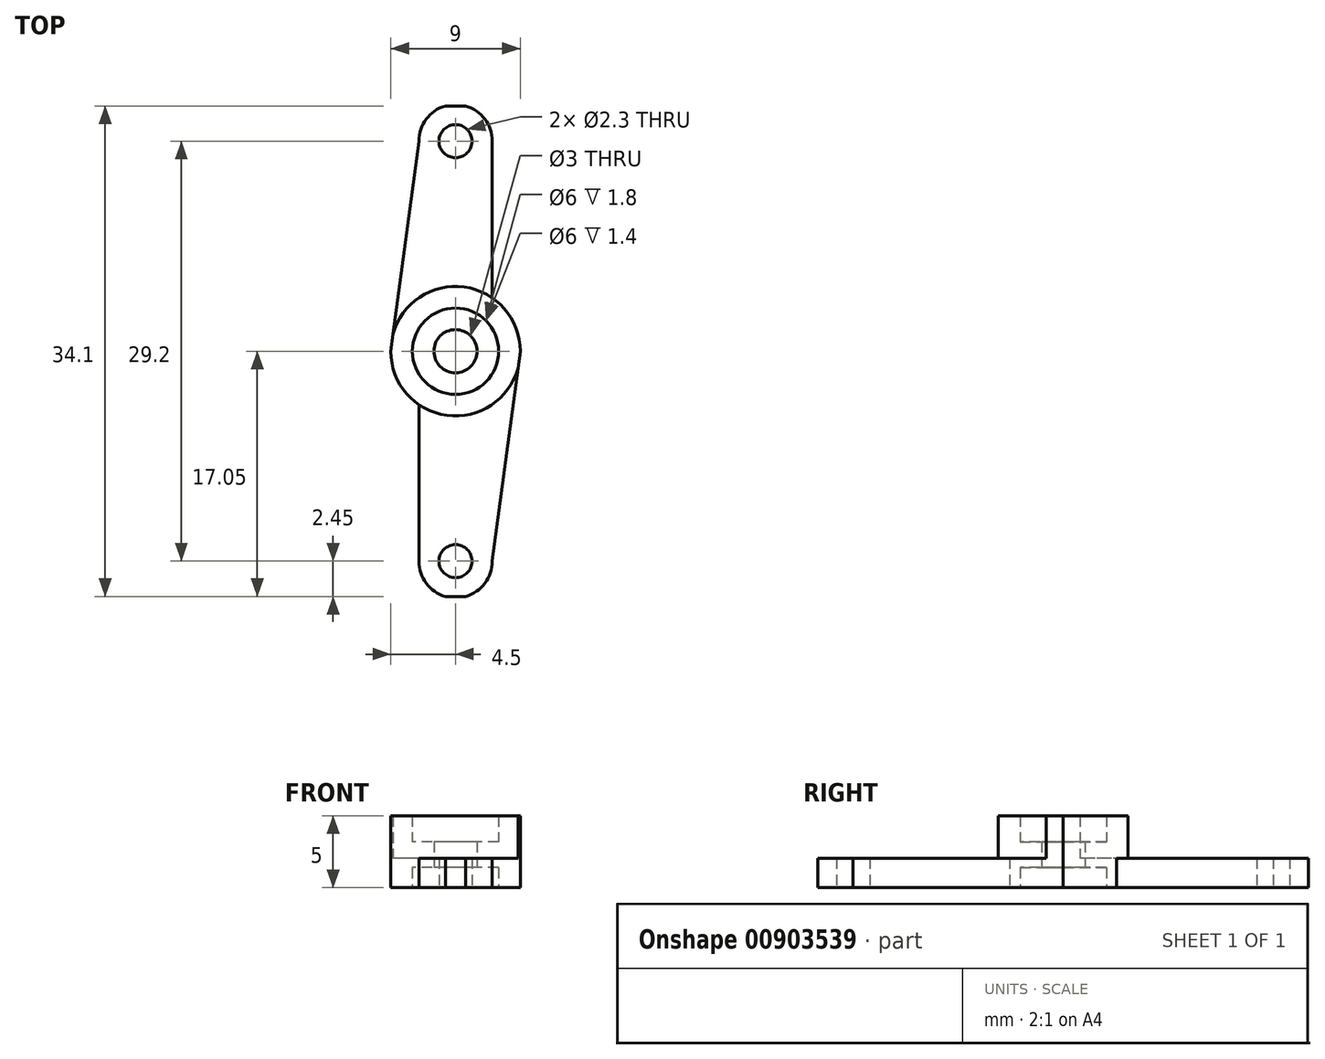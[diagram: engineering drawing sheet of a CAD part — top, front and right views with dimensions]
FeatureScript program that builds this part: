
annotation { "Feature Type Name" : "Feature", "Feature Type Description" : "" }
export const myFeature = defineFeature(function(context is Context, id is Id, definition is map)
    precondition{}
    {
        {
            var Q0;
            Q0=qCreatedBy(makeId("Top.planeOp"),FACE);
            var sketch = newSketch(context, id + "F0", { "sketchPlane" : qUnion([Q0])});
            skLineSegment(sketch, "E0.bottom", {"start": v(4.5, -17.05) * mm, "end": v(-4.5, -17.05) * mm});
            skLineSegment(sketch, "E0.top", {"start": v(4.5, 17.05) * mm, "end": v(-4.5, 17.05) * mm});
            skLineSegment(sketch, "E0.left", {"start": v(4.5, -17.05) * mm, "end": v(4.5, 17.05) * mm});
            skLineSegment(sketch, "E0.right", {"start": v(-4.5, -17.05) * mm, "end": v(-4.5, 17.05) * mm});
            skPoint(sketch, "E0.middle", {"position": v(0, 0) * mm});
            skCircle(sketch, "E1", {"center": v(0, 0) * mm, "radius": 4.5 * mm});
            skLineSegment(sketch, "E2", {"start": v(0, 0) * mm, "end": v(0, -14.6) * mm});
            skLineSegment(sketch, "E3", {"start": v(0, 0) * mm, "end": v(0, 14.6) * mm});
            skCircle(sketch, "E4", {"center": v(0, 14.6) * mm, "radius": 1.15 * mm});
            skCircle(sketch, "E5", {"center": v(0, -14.6) * mm, "radius": 1.15 * mm});
            skCircle(sketch, "E6.0", {"center": v(0, 14.6) * mm, "radius": 2.55 * mm});
            skCircle(sketch, "E7.0", {"center": v(0, -14.6) * mm, "radius": 2.55 * mm});
            skLineSegment(sketch, "E8", {"start": v(2.55, 14.6) * mm, "end": v(2.55, 3.7) * mm});
            skLineSegment(sketch, "E9", {"start": v(-2.55, -14.6) * mm, "end": v(-2.55, -3.7) * mm});
            skLineSegment(sketch, "E10", {"start": v(-2.55, -14.6) * mm, "end": v(2.55, -14.6) * mm, "construction": true});
            skLineSegment(sketch, "E11", {"start": v(2.55, 14.6) * mm, "end": v(-2.55, 14.6) * mm, "construction": true});
            skLineSegment(sketch, "E12", {"start": v(2.55, -14.6) * mm, "end": v(4.5, 0) * mm});
            skLineSegment(sketch, "E13", {"start": v(-2.55, 14.6) * mm, "end": v(-4.5, 0) * mm});
            skCircle(sketch, "E14", {"center": v(0, 0) * mm, "radius": 3 * mm});
            skCircle(sketch, "E15", {"center": v(0, 0) * mm, "radius": 1.5 * mm});
            skSolve(sketch);
        }
        {
            var Q0;
            {var subQ0=sQuery(id+"F0.wireOp",EDGE,"E2");var subQ1=sQuery(id+"F0.wireOp",EDGE,"E1");var subQ2=makeQuery(id+"F0.imprint","INTERSECT",VERTEX,{"derivedFrom":[subQ1,subQ0]});Q0=makeQuery(id+"F0.imprint","IMPRINT",FACE,{"disambiguationData":[TD([[makeQuery(id+"F0.imprint","IMPRINT",EDGE,{"disambiguationData":[TD([[subQ2,-1.0]])],"derivedFrom":subQ1}),-1.0]])]});}
            var Q1;
            Q1=makeQuery(id+"F0.imprint","IMPRINT",FACE,{"disambiguationData":[TD([[makeQuery(id+"F0.imprint","IMPRINT",EDGE,{"derivedFrom":sQuery(id+"F0.wireOp",EDGE,"E5")}),-1.0]])]});
            var Q2;
            {var subQ0=sQuery(id+"F0.wireOp",EDGE,"E9");Q2=makeQuery(id+"F0.imprint","IMPRINT",FACE,{"disambiguationData":[TD([[makeQuery(id+"F0.imprint","IMPRINT",EDGE,{"derivedFrom":subQ0}),-1.0]])]});}
            var Q3;
            {var subQ1=sQuery(id+"F0.wireOp",EDGE,"E1");var subQ8=sQuery(id+"F0.wireOp",EDGE,"E3");var subQ9=makeQuery(id+"F0.imprint","INTERSECT",VERTEX,{"derivedFrom":[subQ1,subQ8]});Q3=makeQuery(id+"F0.imprint","IMPRINT",FACE,{"disambiguationData":[TD([[makeQuery(id+"F0.imprint","IMPRINT",EDGE,{"disambiguationData":[TD([[subQ9,-1.0]])],"derivedFrom":subQ1}),1.0]])]});}
            var Q4;
            {var subQ0=sQuery(id+"F0.wireOp",EDGE,"E15");var subQ1=sQuery(id+"F0.wireOp",EDGE,"E2");var subQ2=makeQuery(id+"F0.imprint","INTERSECT",VERTEX,{"derivedFrom":[subQ1,subQ0]});Q4=makeQuery(id+"F0.imprint","IMPRINT",FACE,{"disambiguationData":[TD([[makeQuery(id+"F0.imprint","IMPRINT",EDGE,{"disambiguationData":[TD([[subQ2,-1.0]])],"derivedFrom":subQ1}),-1.0]])]});}
            var Q5;
            {var subQ0=sQuery(id+"F0.wireOp",EDGE,"E3");var subQ1=sQuery(id+"F0.wireOp",EDGE,"E1");var subQ2=makeQuery(id+"F0.imprint","INTERSECT",VERTEX,{"derivedFrom":[subQ1,subQ0]});Q5=makeQuery(id+"F0.imprint","IMPRINT",FACE,{"disambiguationData":[TD([[makeQuery(id+"F0.imprint","IMPRINT",EDGE,{"disambiguationData":[TD([[subQ2,-1.0]])],"derivedFrom":subQ1}),-1.0]])]});}
            var Q6;
            {var subQ0=sQuery(id+"F0.wireOp",EDGE,"E8");Q6=makeQuery(id+"F0.imprint","IMPRINT",FACE,{"disambiguationData":[TD([[makeQuery(id+"F0.imprint","IMPRINT",EDGE,{"derivedFrom":subQ0}),-1.0]])]});}
            var Q7;
            Q7=makeQuery(id+"F0.imprint","IMPRINT",FACE,{"disambiguationData":[TD([[makeQuery(id+"F0.imprint","IMPRINT",EDGE,{"derivedFrom":sQuery(id+"F0.wireOp",EDGE,"E4")}),-1.0]])]});
            var Q8;
            {var subQ1=sQuery(id+"F0.wireOp",EDGE,"E1");var subQ5=makeQuery(id+"F0.imprint","INTERSECT",VERTEX,{"derivedFrom":[subQ1,sQuery(id+"F0.wireOp",EDGE,"E8")]});Q8=makeQuery(id+"F0.imprint","IMPRINT",FACE,{"disambiguationData":[TD([[makeQuery(id+"F0.imprint","IMPRINT",EDGE,{"disambiguationData":[TD([[subQ5,-1.0]])],"derivedFrom":subQ1}),1.0]])]});}
            var Q9;
            {var subQ0=sQuery(id+"F0.wireOp",EDGE,"E15");var subQ1=sQuery(id+"F0.wireOp",EDGE,"E2");var subQ2=makeQuery(id+"F0.imprint","INTERSECT",VERTEX,{"derivedFrom":[subQ1,subQ0]});Q9=makeQuery(id+"F0.imprint","IMPRINT",FACE,{"disambiguationData":[TD([[makeQuery(id+"F0.imprint","IMPRINT",EDGE,{"disambiguationData":[TD([[subQ2,-1.0]])],"derivedFrom":subQ1}),1.0]])]});}
            extrude(context, id + "F1", {"entities" : qUnion([Q0, Q1, Q2, Q3, Q4, Q5, Q6, Q7, Q8, Q9]), "depth" : 2.06 * mm, "offsetDistance" : 25 * mm});
        }
        {
            var Q0;
            {var subQ0=sQuery(id+"F0.wireOp",EDGE,"E15");var subQ1=sQuery(id+"F0.wireOp",EDGE,"E2");var subQ2=makeQuery(id+"F0.imprint","INTERSECT",VERTEX,{"derivedFrom":[subQ1,subQ0]});Q0=makeQuery(id+"F0.imprint","IMPRINT",FACE,{"disambiguationData":[TD([[makeQuery(id+"F0.imprint","IMPRINT",EDGE,{"disambiguationData":[TD([[subQ2,-1.0]])],"derivedFrom":subQ1}),-1.0]])]});}
            var Q1;
            {var subQ0=sQuery(id+"F0.wireOp",EDGE,"E15");var subQ1=sQuery(id+"F0.wireOp",EDGE,"E2");var subQ2=makeQuery(id+"F0.imprint","INTERSECT",VERTEX,{"derivedFrom":[subQ1,subQ0]});Q1=makeQuery(id+"F0.imprint","IMPRINT",FACE,{"disambiguationData":[TD([[makeQuery(id+"F0.imprint","IMPRINT",EDGE,{"disambiguationData":[TD([[subQ2,-1.0]])],"derivedFrom":subQ1}),1.0]])]});}
            extrude(context, id + "F2", {"entities" : qUnion([Q0, Q1]), "operationType" : NewBodyOperationType.ADD, "depth" : 3.2 * mm, "offsetDistance" : 25 * mm});
        }
        {
            var Q0;
            {var subQ1=sQuery(id+"F0.wireOp",EDGE,"E1");var subQ8=sQuery(id+"F0.wireOp",EDGE,"E3");var subQ9=makeQuery(id+"F0.imprint","INTERSECT",VERTEX,{"derivedFrom":[subQ1,subQ8]});Q0=makeQuery(id+"F0.imprint","IMPRINT",FACE,{"disambiguationData":[TD([[makeQuery(id+"F0.imprint","IMPRINT",EDGE,{"disambiguationData":[TD([[subQ9,-1.0]])],"derivedFrom":subQ1}),1.0]])]});}
            var Q1;
            {var subQ1=sQuery(id+"F0.wireOp",EDGE,"E1");var subQ5=makeQuery(id+"F0.imprint","INTERSECT",VERTEX,{"derivedFrom":[subQ1,sQuery(id+"F0.wireOp",EDGE,"E8")]});Q1=makeQuery(id+"F0.imprint","IMPRINT",FACE,{"disambiguationData":[TD([[makeQuery(id+"F0.imprint","IMPRINT",EDGE,{"disambiguationData":[TD([[subQ5,-1.0]])],"derivedFrom":subQ1}),1.0]])]});}
            extrude(context, id + "F3", {"entities" : qUnion([Q0, Q1]), "operationType" : NewBodyOperationType.ADD, "depth" : 5 * mm, "offsetDistance" : 25 * mm});
        }
        {
            var Q0;
            {var subQ0=sQuery(id+"F0.wireOp",EDGE,"E15");var subQ1=sQuery(id+"F0.wireOp",EDGE,"E2");var subQ2=makeQuery(id+"F0.imprint","INTERSECT",VERTEX,{"derivedFrom":[subQ1,subQ0]});Q0=makeQuery(id+"F0.imprint","IMPRINT",FACE,{"disambiguationData":[TD([[makeQuery(id+"F0.imprint","IMPRINT",EDGE,{"disambiguationData":[TD([[subQ2,-1.0]])],"derivedFrom":subQ1}),-1.0]])]});}
            var Q1;
            {var subQ0=sQuery(id+"F0.wireOp",EDGE,"E15");var subQ1=sQuery(id+"F0.wireOp",EDGE,"E2");var subQ2=makeQuery(id+"F0.imprint","INTERSECT",VERTEX,{"derivedFrom":[subQ1,subQ0]});Q1=makeQuery(id+"F0.imprint","IMPRINT",FACE,{"disambiguationData":[TD([[makeQuery(id+"F0.imprint","IMPRINT",EDGE,{"disambiguationData":[TD([[subQ2,-1.0]])],"derivedFrom":subQ1}),1.0]])]});}
            extrude(context, id + "F4", {"entities" : qUnion([Q0, Q1]), "operationType" : NewBodyOperationType.REMOVE, "oppositeDirection" : true, "depth" : -1.4 * mm, "offsetDistance" : 25 * mm});
        }
    });
